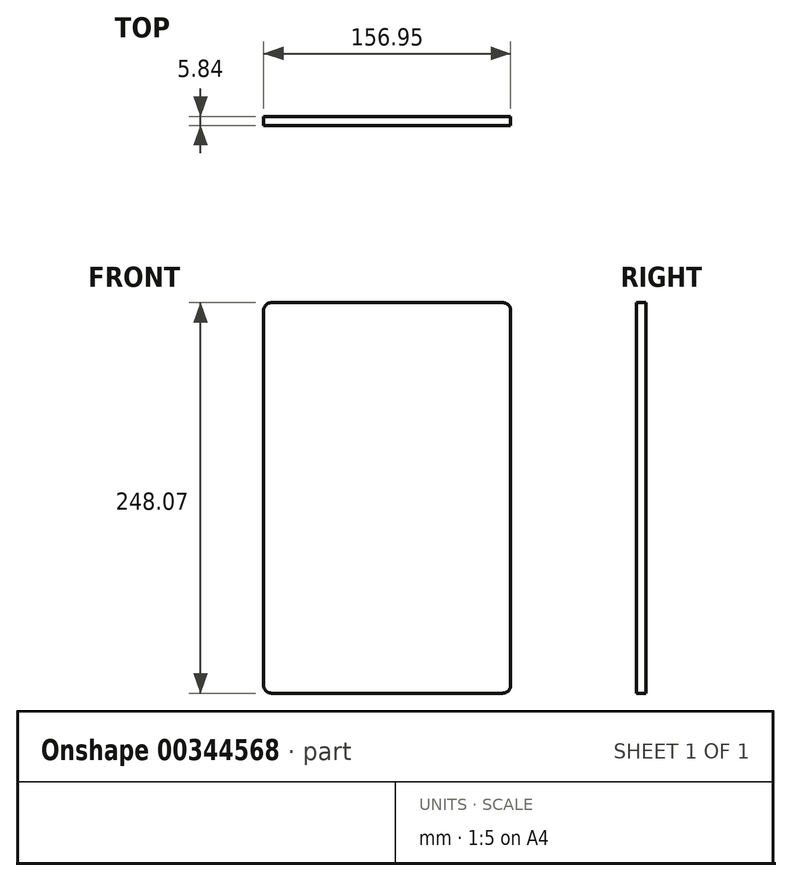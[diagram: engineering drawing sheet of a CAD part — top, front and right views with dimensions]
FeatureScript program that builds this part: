
annotation { "Feature Type Name" : "Feature", "Feature Type Description" : "" }
export const myFeature = defineFeature(function(context is Context, id is Id, definition is map)
    precondition{}
    {
        {
            var Q0;
            Q0=qCreatedBy(makeId("Front.planeOp"),FACE);
            var sketch = newSketch(context, id + "F0", { "sketchPlane" : qUnion([Q0])});
            skLineSegment(sketch, "E0.bottom", {"start": v(0, 0) * mm, "end": v(156.95, 0) * mm});
            skLineSegment(sketch, "E0.top", {"start": v(0, -248.07) * mm, "end": v(156.95, -248.07) * mm});
            skLineSegment(sketch, "E0.left", {"start": v(0, 0) * mm, "end": v(0, -248.07) * mm});
            skLineSegment(sketch, "E0.right", {"start": v(156.95, 0) * mm, "end": v(156.95, -248.07) * mm});
            skSolve(sketch);
        }
        {
            var Q0;
            Q0=makeQuery(id+"F0.imprint","IMPRINT",FACE,{"disambiguationData":[TD([[makeQuery(id+"F0.imprint","IMPRINT",EDGE,{"derivedFrom":sQuery(id+"F0.wireOp",EDGE,"E0.bottom")}),-1.0]])]});
            extrude(context, id + "F1", {"entities" : qUnion([Q0]), "depth" : 5.84 * mm});
        }
        {
            var Q0;
            Q0=makeQuery(id+"F1.opExtrude","SWEPT_EDGE",EDGE,{"disambiguationData":[OSD([sQuery(id+"F0.wireOp",EDGE,"E0.bottom"),sQuery(id+"F0.wireOp",EDGE,"E0.right")])]});
            var Q1;
            Q1=makeQuery(id+"F1.opExtrude","SWEPT_EDGE",EDGE,{"disambiguationData":[OSD([sQuery(id+"F0.wireOp",EDGE,"E0.top"),sQuery(id+"F0.wireOp",EDGE,"E0.left")])]});
            var Q2;
            Q2=makeQuery(id+"F1.opExtrude","SWEPT_EDGE",EDGE,{"disambiguationData":[OSD([sQuery(id+"F0.wireOp",EDGE,"E0.top"),sQuery(id+"F0.wireOp",EDGE,"E0.right")])]});
            var Q3;
            Q3=makeQuery(id+"F1.opExtrude","SWEPT_EDGE",EDGE,{"disambiguationData":[OSD([sQuery(id+"F0.wireOp",EDGE,"E0.bottom"),sQuery(id+"F0.wireOp",EDGE,"E0.left")])]});
            fillet(context, id + "F2", {"entities" : qUnion([Q0, Q1, Q2, Q3]), "radius" : 5.08 * mm, "tangentPropagation" : true, "allowEdgeOverflow" : false});
        }
    });
